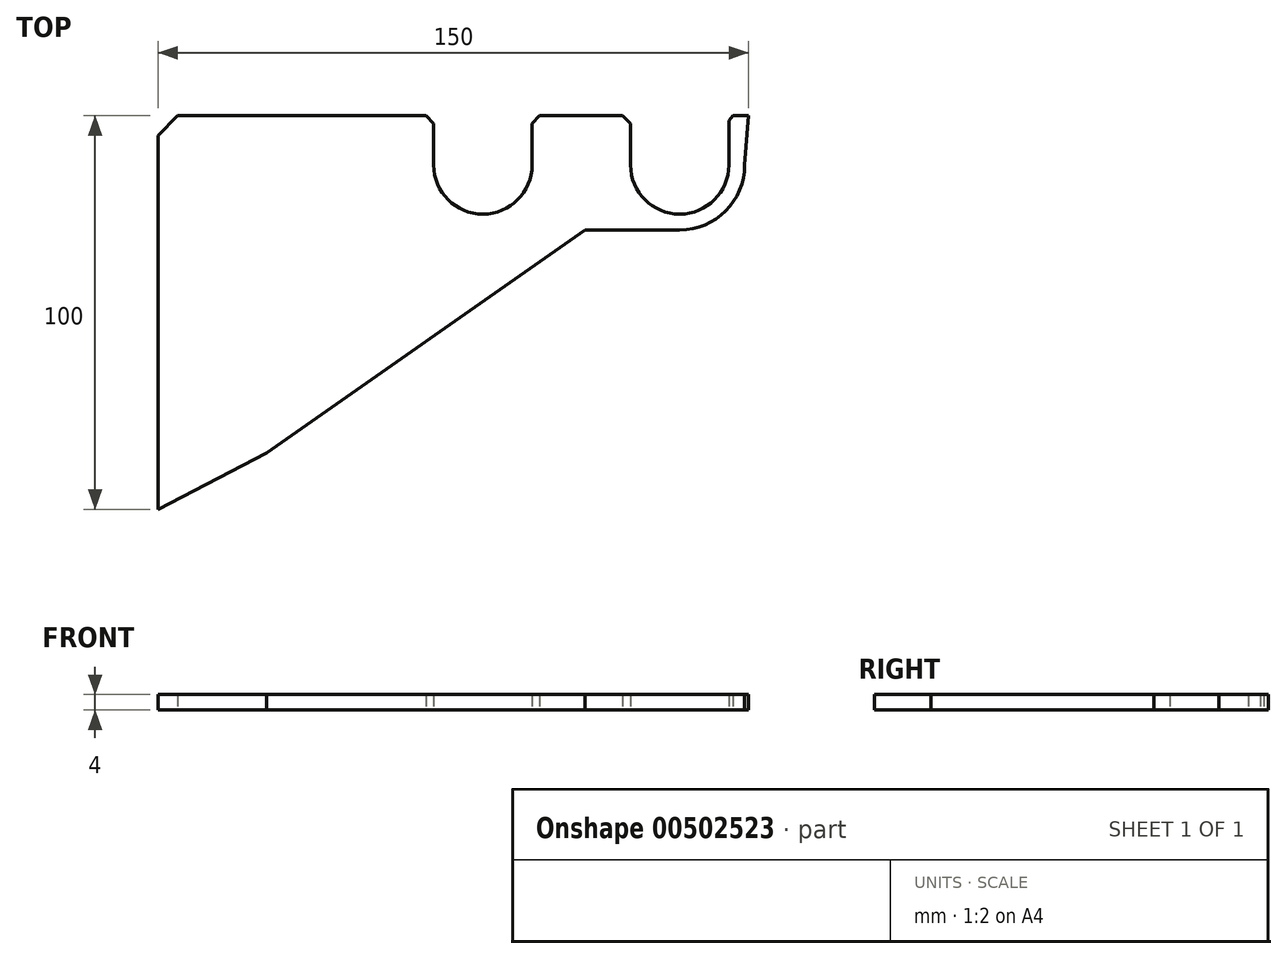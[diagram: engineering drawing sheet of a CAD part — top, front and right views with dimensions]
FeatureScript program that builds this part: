
annotation { "Feature Type Name" : "Feature", "Feature Type Description" : "" }
export const myFeature = defineFeature(function(context is Context, id is Id, definition is map)
    precondition{}
    {
        {
            var Q0;
            Q0=qCreatedBy(makeId("Top.planeOp"),FACE);
            var sketch = newSketch(context, id + "F0", { "sketchPlane" : qUnion([Q0])});
            skLineSegment(sketch, "E0", {"start": v(0, 0) * mm, "end": v(0, -100) * mm, "construction": true});
            skLineSegment(sketch, "E1.top", {"start": v(70, -25) * mm, "end": v(95, -25) * mm, "construction": true});
            skLineSegment(sketch, "E2.top", {"start": v(120, -25) * mm, "end": v(145, -25) * mm, "construction": true});
            skPoint(sketch, "E3.centerSnap0", {"position": v(70, -12.5) * mm});
            skPoint(sketch, "E3.centerSnap1", {"position": v(82.5, -25) * mm});
            skPoint(sketch, "E4.centerSnap0", {"position": v(120, -12.5) * mm});
            skPoint(sketch, "E4.centerSnap1", {"position": v(132.5, -25) * mm});
            skPoint(sketch, "E5", {"position": v(5, 0) * mm});
            skPoint(sketch, "E6", {"position": v(0, -5) * mm});
            skLineSegment(sketch, "E7", {"start": v(0, -5) * mm, "end": v(5, 0) * mm});
            skArc(sketch, "E8", {"start": v(70, -12.5) * mm, "mid": v(82.5, -25) * mm, "end": v(95, -12.5) * mm});
            skArc(sketch, "E9", {"start": v(120, -12.5) * mm, "mid": v(132.5, -25) * mm, "end": v(145, -12.5) * mm});
            skLineSegment(sketch, "E10", {"start": v(0, -5) * mm, "end": v(0, -100) * mm});
            skLineSegment(sketch, "E11", {"start": v(145, -3.33) * mm, "end": v(145, -12.5) * mm});
            skArc(sketch, "E12.0", {"start": v(116, -12.5) * mm, "mid": v(132.5, -29) * mm, "end": v(149, -12.5) * mm});
            skLineSegment(sketch, "E13", {"start": v(150, 0) * mm, "end": v(149, -12.5) * mm});
            skPoint(sketch, "E14", {"position": v(68, 0) * mm});
            skPoint(sketch, "E15", {"position": v(70, -2) * mm});
            skPoint(sketch, "E16", {"position": v(95, -2) * mm});
            skPoint(sketch, "E17", {"position": v(96.86, 0) * mm});
            skLineSegment(sketch, "E18", {"start": v(5, 0) * mm, "end": v(68, 0) * mm});
            skLineSegment(sketch, "E19", {"start": v(68, 0) * mm, "end": v(70, -2) * mm});
            skLineSegment(sketch, "E20", {"start": v(70, -2) * mm, "end": v(70, -12.5) * mm});
            skLineSegment(sketch, "E21", {"start": v(95, -12.5) * mm, "end": v(95, -2) * mm});
            skLineSegment(sketch, "E22", {"start": v(95, -2) * mm, "end": v(96.86, 0) * mm});
            skPoint(sketch, "E23", {"position": v(118, 0) * mm});
            skPoint(sketch, "E24", {"position": v(120, -2) * mm});
            skPoint(sketch, "E25", {"position": v(145.97, 0) * mm});
            skPoint(sketch, "E26", {"position": v(145, -1.16) * mm});
            skLineSegment(sketch, "E27", {"start": v(145, -1.16) * mm, "end": v(145, -3.33) * mm});
            skLineSegment(sketch, "E28", {"start": v(145, -1.16) * mm, "end": v(145.97, 0) * mm});
            skLineSegment(sketch, "E29", {"start": v(145.97, 0) * mm, "end": v(150, 0) * mm});
            skLineSegment(sketch, "E30", {"start": v(27.49, -85.7) * mm, "end": v(0, -100) * mm});
            skLineSegment(sketch, "E31", {"start": v(132.5, -29) * mm, "end": v(108.43, -29) * mm});
            skPoint(sketch, "E31.endSnap0", {"position": v(108.43, 0) * mm});
            skLineSegment(sketch, "E32", {"start": v(27.49, -85.7) * mm, "end": v(108.43, -29) * mm});
            skLineSegment(sketch, "E33", {"start": v(96.86, 0) * mm, "end": v(118, 0) * mm});
            skLineSegment(sketch, "E34", {"start": v(120, -2) * mm, "end": v(118, 0) * mm});
            skLineSegment(sketch, "E35", {"start": v(120, -12.5) * mm, "end": v(120, -2) * mm});
            skSolve(sketch);
        }
        {
            var Q0;
            Q0=makeQuery(id+"F0.imprint","IMPRINT",FACE,{"disambiguationData":[TD([[makeQuery(id+"F0.imprint","IMPRINT",EDGE,{"derivedFrom":sQuery(id+"F0.wireOp",EDGE,"E7")}),-1.0]])]});
            extrude(context, id + "F1", {"entities" : qUnion([Q0]), "depth" : 4 * mm});
        }
    });
